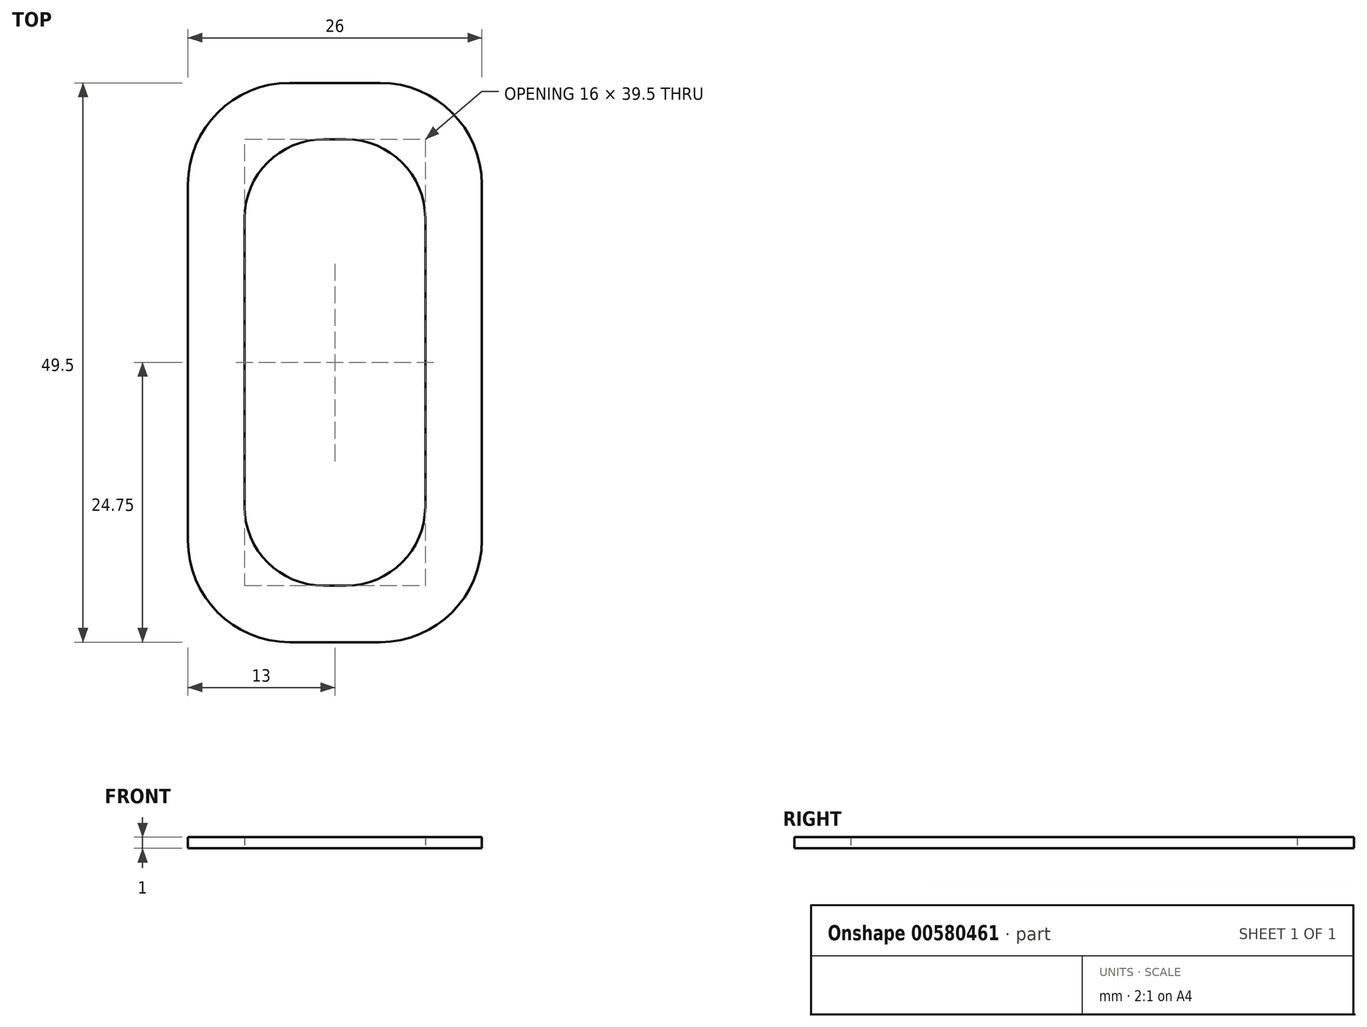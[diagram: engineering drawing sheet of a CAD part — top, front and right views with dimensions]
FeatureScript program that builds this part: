
annotation { "Feature Type Name" : "Feature", "Feature Type Description" : "" }
export const myFeature = defineFeature(function(context is Context, id is Id, definition is map)
    precondition{}
    {
        {
            var Q0;
            Q0=qCreatedBy(makeId("Top.planeOp"),FACE);
            var sketch = newSketch(context, id + "F0", { "sketchPlane" : qUnion([Q0])});
            skLineSegment(sketch, "E0.bottom", {"start": v(13, -24.75) * mm, "end": v(-13, -24.75) * mm});
            skLineSegment(sketch, "E0.top", {"start": v(13, 24.75) * mm, "end": v(-13, 24.75) * mm});
            skLineSegment(sketch, "E0.left", {"start": v(13, -24.75) * mm, "end": v(13, 24.75) * mm});
            skLineSegment(sketch, "E0.right", {"start": v(-13, -24.75) * mm, "end": v(-13, 24.75) * mm});
            skPoint(sketch, "E0.middle", {"position": v(0, 0) * mm});
            skLineSegment(sketch, "E1.bottom", {"start": v(8, -19.75) * mm, "end": v(-8, -19.75) * mm});
            skLineSegment(sketch, "E1.top", {"start": v(8, 19.75) * mm, "end": v(-8, 19.75) * mm});
            skLineSegment(sketch, "E1.left", {"start": v(8, -19.75) * mm, "end": v(8, 19.75) * mm});
            skLineSegment(sketch, "E1.right", {"start": v(-8, -19.75) * mm, "end": v(-8, 19.75) * mm});
            skSolve(sketch);
        }
        {
            var Q0;
            Q0 = qSketchRegion(id + "F0", true);
            extrude(context, id + "F1", {"entities" : qUnion([Q0]), "depth" : 1 * mm, "offsetDistance" : 25 * mm});
        }
        {
            var Q0;
            Q0=makeQuery(id+"F1.opExtrude","SWEPT_EDGE",EDGE,{"disambiguationData":[OSD([sQuery(id+"F0.wireOp",EDGE,"E0.top"),sQuery(id+"F0.wireOp",EDGE,"E0.right")])]});
            var Q1;
            Q1=makeQuery(id+"F1.opExtrude","SWEPT_EDGE",EDGE,{"disambiguationData":[OSD([sQuery(id+"F0.wireOp",EDGE,"E0.top"),sQuery(id+"F0.wireOp",EDGE,"E0.left")])]});
            var Q2;
            Q2=makeQuery(id+"F1.opExtrude","SWEPT_EDGE",EDGE,{"disambiguationData":[OSD([sQuery(id+"F0.wireOp",EDGE,"E0.bottom"),sQuery(id+"F0.wireOp",EDGE,"E0.left")])]});
            var Q3;
            Q3=makeQuery(id+"F1.opExtrude","SWEPT_EDGE",EDGE,{"disambiguationData":[OSD([sQuery(id+"F0.wireOp",EDGE,"E0.bottom"),sQuery(id+"F0.wireOp",EDGE,"E0.right")])]});
            fillet(context, id + "F2", {"entities" : qUnion([Q0, Q1, Q2, Q3]), "radius" : 9 * mm, "tangentPropagation" : true, "allowEdgeOverflow" : false});
        }
        {
            var Q0;
            Q0=makeQuery(id+"F1.opExtrude","SWEPT_EDGE",EDGE,{"disambiguationData":[OSD([sQuery(id+"F0.wireOp",EDGE,"E1.bottom"),sQuery(id+"F0.wireOp",EDGE,"E1.right")])]});
            var Q1;
            Q1=makeQuery(id+"F1.opExtrude","SWEPT_EDGE",EDGE,{"disambiguationData":[OSD([sQuery(id+"F0.wireOp",EDGE,"E1.top"),sQuery(id+"F0.wireOp",EDGE,"E1.right")])]});
            var Q2;
            Q2=makeQuery(id+"F1.opExtrude","SWEPT_EDGE",EDGE,{"disambiguationData":[OSD([sQuery(id+"F0.wireOp",EDGE,"E1.top"),sQuery(id+"F0.wireOp",EDGE,"E1.left")])]});
            var Q3;
            Q3=makeQuery(id+"F1.opExtrude","SWEPT_EDGE",EDGE,{"disambiguationData":[OSD([sQuery(id+"F0.wireOp",EDGE,"E1.bottom"),sQuery(id+"F0.wireOp",EDGE,"E1.left")])]});
            fillet(context, id + "F3", {"entities" : qUnion([Q0, Q1, Q2, Q3]), "radius" : 7 * mm, "tangentPropagation" : true, "allowEdgeOverflow" : false});
        }
    });
